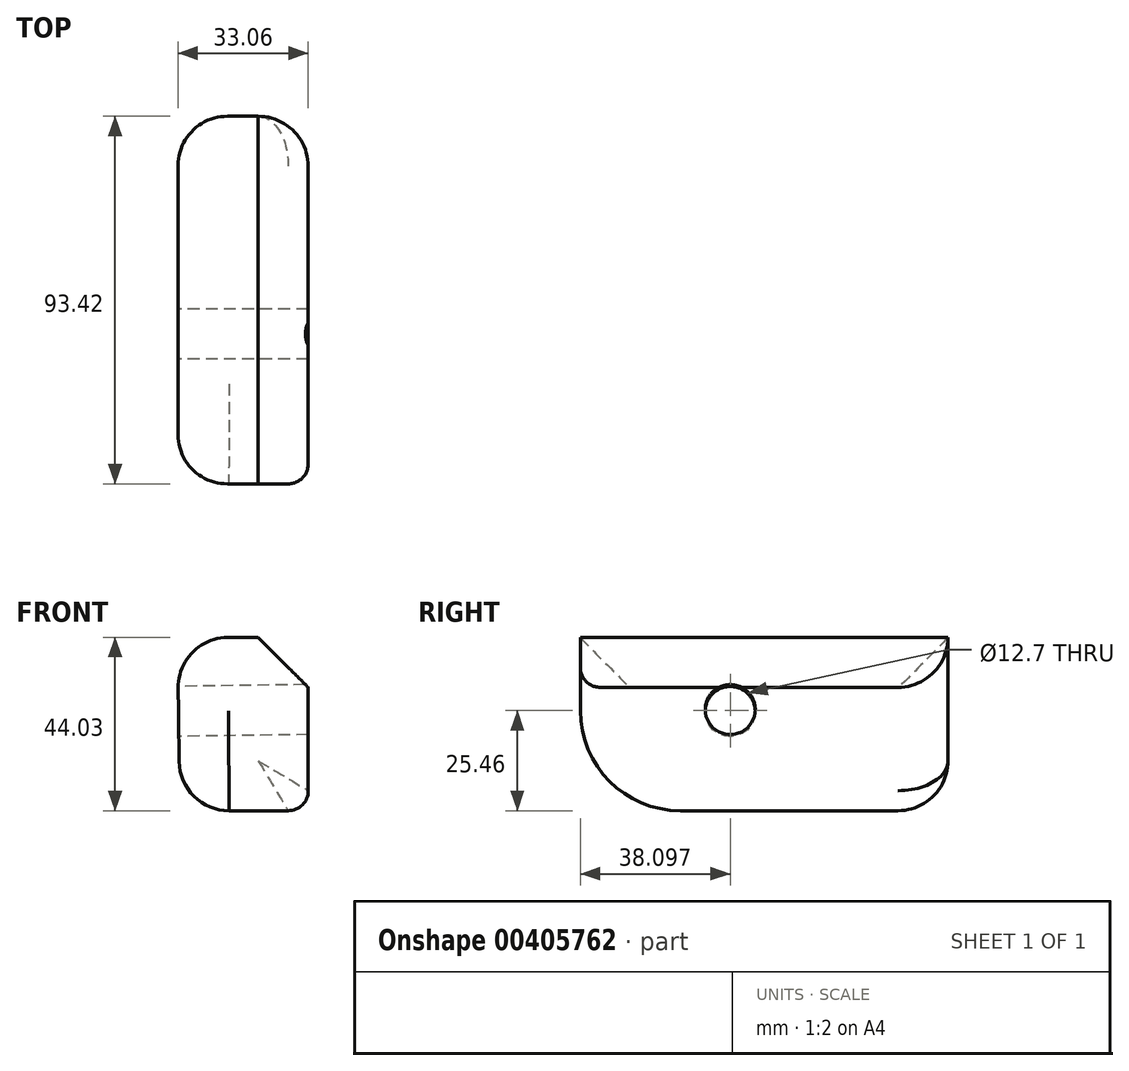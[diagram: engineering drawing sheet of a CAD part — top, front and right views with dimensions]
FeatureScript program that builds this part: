
annotation { "Feature Type Name" : "Feature", "Feature Type Description" : "" }
export const myFeature = defineFeature(function(context is Context, id is Id, definition is map)
    precondition{}
    {
        {
            var Q0;
            Q0=qCreatedBy(makeId("Front.planeOp"),FACE);
            var sketch = newSketch(context, id + "F0", { "sketchPlane" : qUnion([Q0])});
            skLineSegment(sketch, "E0.bottom", {"start": v(15.57, 51.57) * mm, "end": v(48.8, 51.57) * mm});
            skLineSegment(sketch, "E0.top", {"start": v(16.19, 7.54) * mm, "end": v(48.8, 7.54) * mm});
            skLineSegment(sketch, "E0.right", {"start": v(48.8, 51.57) * mm, "end": v(48.8, 7.54) * mm});
            skLineSegment(sketch, "E1", {"start": v(15.57, 51.57) * mm, "end": v(16.19, 7.54) * mm});
            skSolve(sketch);
        }
        {
            var Q0;
            Q0 = qSketchRegion(id + "F0", true);
            extrude(context, id + "F1", {"entities" : qUnion([Q0]), "depth" : 93.42 * mm});
        }
        {
            var Q0;
            Q0=makeQuery(id+"F1.opExtrude","CAP_EDGE",EDGE,{"disambiguationData":[OSD([sQuery(id+"F0.wireOp",EDGE,"E0.top")])],"isStart":false});
            fillet(context, id + "F2", {"entities" : qUnion([Q0]), "radius" : 25.4 * mm, "tangentPropagation" : true, "allowEdgeOverflow" : false});
        }
        {
            var Q0;
            Q0=makeQuery(id+"F1.opExtrude","SWEPT_EDGE",EDGE,{"disambiguationData":[OSD([sQuery(id+"F0.wireOp",EDGE,"E0.bottom"),sQuery(id+"F0.wireOp",EDGE,"E0.right")])]});
            chamfer(context, id + "F3", {"entities" : qUnion([Q0]), "width" : 12.7 * mm, "tangentPropagation" : true});
        }
        {
            var Q0;
            Q0=makeQuery(id+"F1.opExtrude","SWEPT_EDGE",EDGE,{"disambiguationData":[OSD([sQuery(id+"F0.wireOp",EDGE,"E0.top"),sQuery(id+"F0.wireOp",EDGE,"E0.right")])]});
            fillet(context, id + "F4", {"entities" : qUnion([Q0]), "radius" : 5.08 * mm, "tangentPropagation" : true, "allowEdgeOverflow" : false});
        }
        {
            var Q0;
            Q0=makeQuery(id+"F1.opExtrude","SWEPT_FACE",FACE,{"disambiguationData":[OSD([sQuery(id+"F0.wireOp",EDGE,"E1")])]});
            var Q1;
            Q1=makeQuery(id+"F1.opExtrude","CAP_EDGE",EDGE,{"disambiguationData":[OSD([sQuery(id+"F0.wireOp",EDGE,"E0.right")])],"isStart":true});
            fillet(context, id + "F5", {"entities" : qUnion([Q0, Q1]), "radius" : 12.7 * mm, "tangentPropagation" : true, "allowEdgeOverflow" : false});
        }
        {
            var Q0;
            Q0=makeQuery(id+"F1.opExtrude","SWEPT_FACE",FACE,{"disambiguationData":[OSD([sQuery(id+"F0.wireOp",EDGE,"E1")])]});
            var sketch = newSketch(context, id + "F6", { "sketchPlane" : qUnion([Q0])});
            skPoint(sketch, "E2", {"position": v(55.32, 32.54) * mm});
            skSolve(sketch);
        }
        {
            var Q0;
            Q0=sQuery(id+"F6.wireOp",VERTEX,"E2");
            var Q1;
            Q1=makeQuery(id+"F1.opExtrude","SWEPT_BODY",BODY,{"disambiguationData":[OSD([sQuery(id+"F0.wireOp",EDGE,"E0.bottom"),sQuery(id+"F0.wireOp",EDGE,"E0.top"),sQuery(id+"F0.wireOp",EDGE,"E0.right"),sQuery(id+"F0.wireOp",EDGE,"E1")])]});
            hole(context, id + "F7", {"style" : HoleStyle.SIMPLE, "endStyle" : HoleEndStyle.THROUGH, "holeDiameter" : 12.7 * mm, "isTappedThrough" : true, "tappedDepth" : 12.7 * mm, "tapClearance" : 3, "locations" : qUnion([Q0]), "scope" : qUnion([Q1])});
        }
    });
